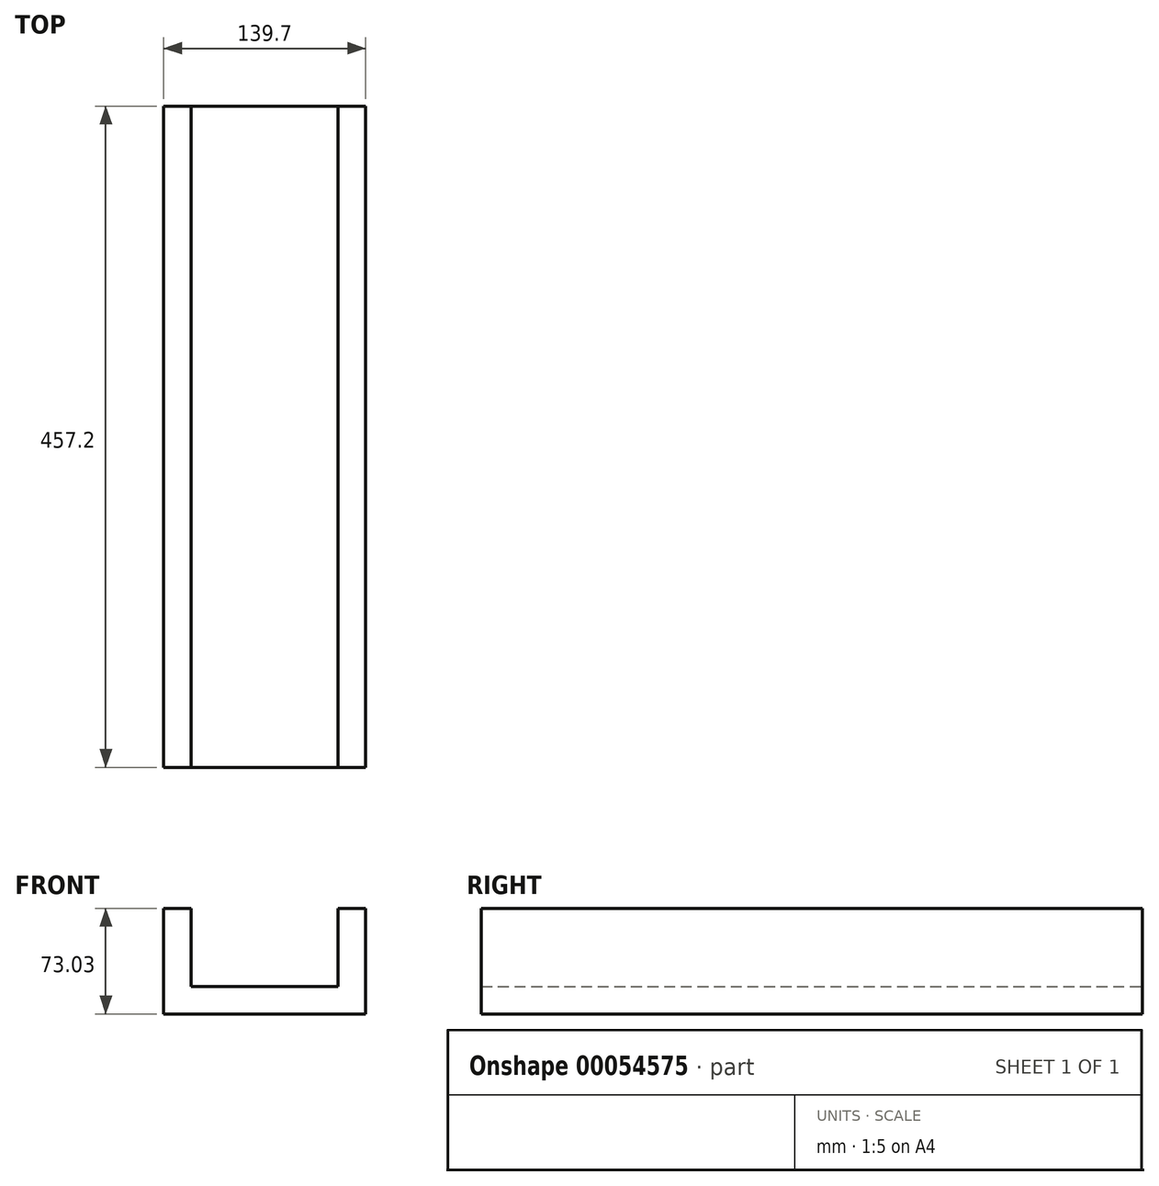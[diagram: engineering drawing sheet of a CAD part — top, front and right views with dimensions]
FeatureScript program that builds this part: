
annotation { "Feature Type Name" : "Feature", "Feature Type Description" : "" }
export const myFeature = defineFeature(function(context is Context, id is Id, definition is map)
    precondition{}
    {
        {
            var Q0;
            Q0=qCreatedBy(makeId("Front.planeOp"),FACE);
            var sketch = newSketch(context, id + "F0", { "sketchPlane" : qUnion([Q0])});
            skLineSegment(sketch, "E0.bottom", {"start": v(0, 0) * mm, "end": v(139.7, 0) * mm});
            skLineSegment(sketch, "E0.top", {"start": v(0, 19.05) * mm, "end": v(139.7, 19.05) * mm});
            skLineSegment(sketch, "E0.left", {"start": v(0, 0) * mm, "end": v(0, 19.05) * mm});
            skLineSegment(sketch, "E0.right", {"start": v(139.7, 0) * mm, "end": v(139.7, 19.05) * mm});
            skSolve(sketch);
        }
        {
            var Q0;
            Q0 = qSketchRegion(id + "F0", true);
            extrude(context, id + "F1", {"entities" : qUnion([Q0]), "depth" : 457.2 * mm});
        }
        {
            var Q0;
            Q0=makeQuery(id+"F1.opExtrude","SWEPT_FACE",FACE,{"disambiguationData":[OSD([sQuery(id+"F0.wireOp",EDGE,"E0.top")])]});
            var sketch = newSketch(context, id + "F2", { "sketchPlane" : qUnion([Q0])});
            skLineSegment(sketch, "E1.bottom", {"start": v(139.7, -457.2) * mm, "end": v(120.65, -457.2) * mm});
            skLineSegment(sketch, "E1.top", {"start": v(139.7, 0) * mm, "end": v(120.65, 0) * mm});
            skLineSegment(sketch, "E1.left", {"start": v(139.7, -457.2) * mm, "end": v(139.7, 0) * mm});
            skLineSegment(sketch, "E1.right", {"start": v(120.65, -457.2) * mm, "end": v(120.65, 0) * mm});
            skSolve(sketch);
        }
        {
            var Q0;
            Q0=makeQuery(id+"F2.imprint","IMPRINT",FACE,{"disambiguationData":[TD([[makeQuery(id+"F2.imprint","IMPRINT",EDGE,{"derivedFrom":sQuery(id+"F2.wireOp",EDGE,"E1.bottom")}),1.0]])]});
            extrude(context, id + "F3", {"entities" : qUnion([Q0]), "operationType" : NewBodyOperationType.ADD, "depth" : 53.97 * mm});
        }
        {
            var Q0;
            Q0=makeQuery(id+"F1.opExtrude","SWEPT_FACE",FACE,{"disambiguationData":[OSD([sQuery(id+"F0.wireOp",EDGE,"E0.top")])]});
            var sketch = newSketch(context, id + "F4", { "sketchPlane" : qUnion([Q0])});
            skLineSegment(sketch, "E2.bottom", {"start": v(0, -457.2) * mm, "end": v(19.05, -457.2) * mm});
            skLineSegment(sketch, "E2.top", {"start": v(0, 0) * mm, "end": v(19.05, 0) * mm});
            skLineSegment(sketch, "E2.left", {"start": v(0, -457.2) * mm, "end": v(0, 0) * mm});
            skLineSegment(sketch, "E2.right", {"start": v(19.05, -457.2) * mm, "end": v(19.05, 0) * mm});
            skSolve(sketch);
        }
        {
            var Q0;
            Q0 = qSketchRegion(id + "F4", true);
            extrude(context, id + "F5", {"entities" : qUnion([Q0]), "operationType" : NewBodyOperationType.ADD, "depth" : 53.97 * mm});
        }
    });
